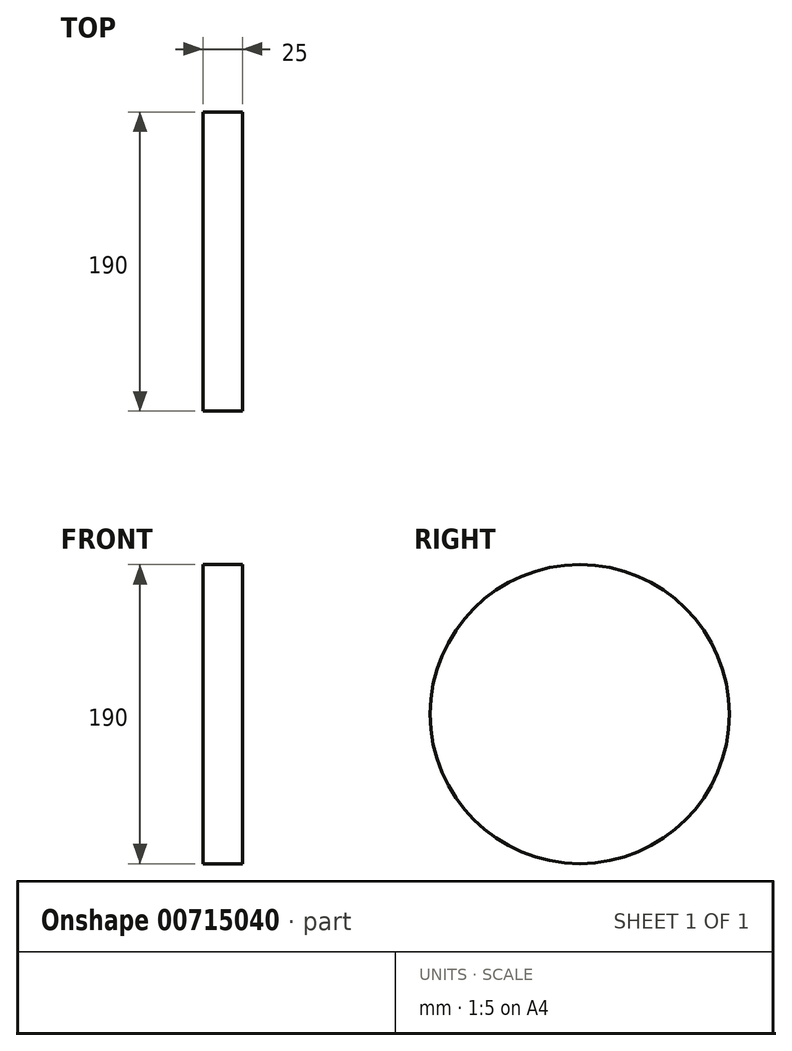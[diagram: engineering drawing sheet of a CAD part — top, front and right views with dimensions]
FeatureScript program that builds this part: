
annotation { "Feature Type Name" : "Feature", "Feature Type Description" : "" }
export const myFeature = defineFeature(function(context is Context, id is Id, definition is map)
    precondition{}
    {
        {
            var Q0;
            Q0=qCreatedBy(makeId("Right.planeOp"),FACE);
            var sketch = newSketch(context, id + "F0", { "sketchPlane" : qUnion([Q0])});
            skCircle(sketch, "E0", {"center": v(0, 0) * mm, "radius": 95 * mm});
            skSolve(sketch);
        }
        {
            var Q0;
            Q0=makeQuery(id+"F0.imprint","IMPRINT",FACE,{"disambiguationData":[TD([[makeQuery(id+"F0.imprint","IMPRINT",EDGE,{"derivedFrom":sQuery(id+"F0.wireOp",EDGE,"E0")}),1.0]])]});
            extrude(context, id + "F1", {"entities" : qUnion([Q0]), "depth" : 25 * mm, "offsetDistance" : 25 * mm});
        }
    });
